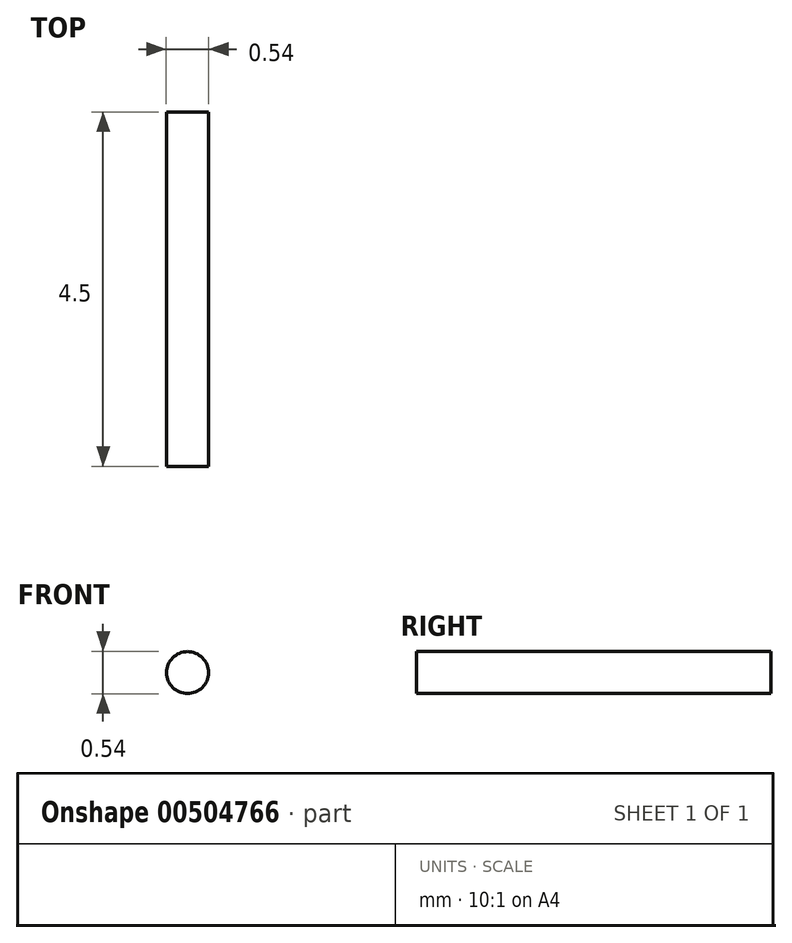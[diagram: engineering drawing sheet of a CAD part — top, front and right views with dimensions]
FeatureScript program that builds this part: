
annotation { "Feature Type Name" : "Feature", "Feature Type Description" : "" }
export const myFeature = defineFeature(function(context is Context, id is Id, definition is map)
    precondition{}
    {
        {
            var Q0;
            Q0=qCreatedBy(makeId("Front.planeOp"),FACE);
            var sketch = newSketch(context, id + "F0", { "sketchPlane" : qUnion([Q0])});
            skCircle(sketch, "E0", {"center": v(0, 0) * mm, "radius": 0.27 * mm});
            skSolve(sketch);
        }
        {
            var Q0;
            Q0=makeQuery(id+"F0.imprint","IMPRINT",FACE,{"disambiguationData":[TD([[makeQuery(id+"F0.imprint","IMPRINT",EDGE,{"derivedFrom":sQuery(id+"F0.wireOp",EDGE,"E0")}),1.0]])]});
            extrude(context, id + "F1", {"entities" : qUnion([Q0]), "depth" : 4.5 * mm});
        }
    });
